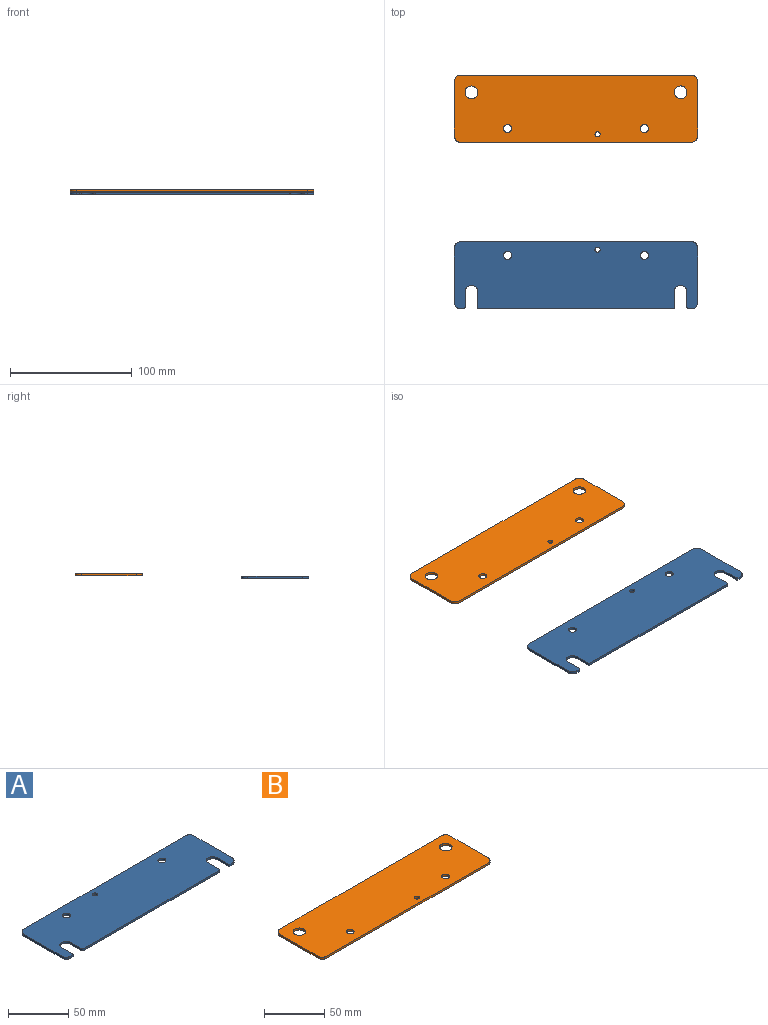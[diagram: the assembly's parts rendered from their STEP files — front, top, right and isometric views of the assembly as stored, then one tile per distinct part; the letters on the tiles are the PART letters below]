
ASSEMBLY  parts=2 mates=1
PART A: 25 faces, bbox 200x55x2 mm
  f0: plane 13x2mm, normal (-1,0,0), area 26mm2, adj f1,f22,f23,f24
  f1: cylinder r=1mm len=2mm, axis (0,0,-1), area 3.1mm2, adj f0,f2,f23,f24
  f2: plane 159.5x2mm, normal (0,-1,0), area 319mm2, adj f1,f3,f23,f24
  f3: cylinder r=1mm len=2mm, axis (0,0,-1), area 3.1mm2, adj f2,f4,f23,f24
  f4: plane 13x2mm, normal (1,0,0), area 26mm2, adj f3,f5,f23,f24
  f5: cylinder r=5.25mm len=10.5mm, axis (0,0,-1), area 33mm2, adj f4,f6,f23,f24
  f6: plane 13x2mm, normal (-1,0,0), area 26mm2, adj f5,f7,f23,f24
  f7: cylinder r=1mm len=2mm, axis (0,0,-1), area 3.1mm2, adj f6,f8,f23,f24
  f8: plane 2.75x2mm, normal (0,-1,0), area 5.5mm2, adj f7,f9,f23,f24
  f9: cylinder r=5mm len=5mm, axis (0,0,-1), area 15.7mm2, adj f8,f10,f23,f24
  f10: plane 45x2mm, normal (1,0,0), area 90mm2, adj f9,f11,f23,f24
  f11: cylinder r=5mm len=5mm, axis (0,0,-1), area 15.7mm2, adj f10,f12,f23,f24
  f12: plane 190x2mm, normal (0,1,0), area 380mm2, adj f11,f13,f23,f24
  f13: cylinder r=5mm len=5mm, axis (0,0,-1), area 15.7mm2, adj f12,f14,f23,f24
  f14: plane 45x2mm, normal (-1,0,0), area 90mm2, adj f13,f15,f23,f24
  f15: cylinder r=5mm len=5mm, axis (0,0,-1), area 15.7mm2, adj f14,f16,f23,f24
  f16: plane 2.75x2mm, normal (0,-1,0), area 5.5mm2, adj f15,f17,f23,f24
  f17: cylinder r=1mm len=2mm, axis (0,0,-1), area 3.1mm2, adj f16,f18,f23,f24
  f18: plane 13x2mm, normal (1,0,0), area 26mm2, adj f17,f22,f23,f24
  f19: cylinder r=3.3mm len=6.6mm, axis (0,0,-1), area 41.5mm2, adj f23,f24
  f20: cylinder r=2.1mm len=4.2mm, axis (0,0,-1), area 26.4mm2, adj f23,f24
  f21: cylinder r=3.3mm len=6.6mm, axis (0,0,-1), area 41.5mm2, adj f23,f24
  f22: cylinder r=5.25mm len=10.5mm, axis (0,0,-1), area 33mm2, adj f0,f18,f23,f24
  f23: plane 200x55mm, normal (0,0,1), area 10514.8mm2, adj f0,f1,f2,f3,f4,f5,f6,f7
  f24: plane 200x55mm, normal (0,0,-1), area 10514.8mm2, adj f0,f1,f2,f3,f4,f5,f6,f7
PART B: 15 faces, bbox 200x55x2 mm
  f0: plane 45x2mm, normal (-1,0,0), area 90mm2, adj f1,f11,f13,f14
  f1: cylinder r=5mm len=5mm, axis (0,0,-1), area 15.7mm2, adj f0,f2,f13,f14
  f2: plane 190x2mm, normal (0,-1,0), area 380mm2, adj f1,f3,f13,f14
  f3: cylinder r=5mm len=5mm, axis (0,0,-1), area 15.7mm2, adj f2,f4,f13,f14
  f4: plane 45x2mm, normal (1,0,0), area 90mm2, adj f3,f5,f13,f14
  f5: cylinder r=5mm len=5mm, axis (0,0,-1), area 15.7mm2, adj f4,f6,f13,f14
  f6: plane 190x2mm, normal (0,1,0), area 380mm2, adj f5,f11,f13,f14
  f7: cylinder r=3.3mm len=6.6mm, axis (0,0,-1), area 41.5mm2, adj f13,f14
  f8: cylinder r=2.1mm len=4.2mm, axis (0,0,-1), area 26.4mm2, adj f13,f14
  f9: cylinder r=3.3mm len=6.6mm, axis (0,0,-1), area 41.5mm2, adj f13,f14
  f10: cylinder r=5.25mm len=10.5mm, axis (0,0,-1), area 66mm2, adj f13,f14
  f11: cylinder r=5mm len=5mm, axis (0,0,-1), area 15.7mm2, adj f0,f6,f13,f14
  f12: cylinder r=5.25mm len=10.5mm, axis (0,0,-1), area 66mm2, adj f13,f14
  f13: plane 200x55mm, normal (0,0,1), area 10723.1mm2, adj f0,f1,f2,f3,f4,f5,f6,f7
  f14: plane 200x55mm, normal (0,0,-1), area 10723.1mm2, adj f0,f1,f2,f3,f4,f5,f6,f7
PLACE A rot(axis=(0,1,0),180deg) t=(-706.06,-187.69,174.45)mm
PLACE B t=(122.52,-195.79,174.54)mm
MATE parallel A.f12 <-> B.f2  axis (0,1,0) through (-291.77,-160.83,173.45)mm
